# Revit family: MD2-OCRX2X2
name_source: partatom
category: Lighting Fixtures
units: mm (PartAtom-declared; Revit-internal decimal feet)

## family parameters
Always vertical = Yes
Cut with Voids When Loaded = No
Host = Ceiling
Light Source = Yes
OmniClass Number = 23.80.70.11.14.17
OmniClass Title = Direct/Indirect
Part Type = Normal
Room Calculation Point = No
Round Connector Dimension = Use Diameter
Shared = No

## types (12) — shared parameters
Assembly Code = D5020200
Color Filter = 16777215
Description = Patient Room Recessed Luminaire with Ambient and Examination Functions
Dimming Lamp Color Temperature Shift = <None>
Emit Shape Visible in Rendering = No
Emit from Rectangle Height = 0' - 1 15/32"
Emit from Rectangle Length = 1' - 11 11/16"
Emit from Rectangle Width = 1' - 11 3/4"
Housing Finish = Metal - Viscor - White
Lamp = LED
Length = 1' - 11 11/16"
Lens Depth = 0' - 1 15/32"
Lens Finish = Acrylic - Viscor - Opal White Square
Manufacturer = CERTOLUX by VISCOR
Model = MD2-OCRX
Tilt Angle = 90.00°
URL = https://www.viscor.com
Voltage = 120 V
Width = 1' - 11 3/4"

## per-type parameters (varying)
| type | Apparent Load | Lamp Wattage | Photometric Web File |
| MD2-OCRX 2X2-LED840K030L-840K040LUNV-C97(2) | 51 VA | 51 VA | MD2-OCRX 2X2-LED840K030L-840K040LUNV-C97(2).ies |
| MD2-OCRX 2X2-LED840K030L-840K050LUNV-C97(2) | 58 VA | 58 VA | MD2-OCRX 2X2-LED840K030L-840K050LUNV-C97(2).ies |
| MD2-OCRX 2X2-LED840K030L-840K060LUNV-C97(2) | 66 VA | 66 VA | MD2-OCRX 2X2-LED840K030L-840K060LUNV-C97(2).ies |
| MD2-OCRX 2X2-LED840K030L-840K075LUNV-C97(2) | 78 VA | 78 VA | MD2-OCRX 2X2-LED840K030L-840K075LUNV-C97(2).ies |
| MD2-OCRX 2X2-LED840K040L-840K040LUNV-C97(2) | 58 VA | 58 VA | MD2-OCRX 2X2-LED840K040L-840K040LUNV-C97(2).ies |
| MD2-OCRX 2X2-LED840K040L-840K050LUNV-C97(2) | 65 VA | 65 VA | MD2-OCRX 2X2-LED840K040L-840K050LUNV-C97(2).ies |
| MD2-OCRX 2X2-LED840K040L-840K060LUNV-C97(2) | 73 VA | 73 VA | MD2-OCRX 2X2-LED840K040L-840K060LUNV-C97(2).ies |
| MD2-OCRX 2X2-LED840K040L-840K075LUNV-C97(2) | 85 VA | 85 VA | MD2-OCRX 2X2-LED840K040L-840K075LUNV-C97(2).ies |
| MD2-OCRX 2X2-LED840K050L-840K040LUNV-C97(2) | 66 VA | 66 VA | MD2-OCRX 2X2-LED840K050L-840K040LUNV-C97(2).ies |
| MD2-OCRX 2X2-LED840K050L-840K050LUNV-C97(2) | 73 VA | 73 VA | MD2-OCRX 2X2-LED840K050L-840K050LUNV-C97(2).ies |
| MD2-OCRX 2X2-LED840K050L-840K060LUNV-C97(2) | 81 VA | 81 VA | MD2-OCRX 2X2-LED840K050L-840K060LUNV-C97(2).ies |
| MD2-OCRX 2X2-LED840K050L-840K075LUNV-C97(2) | 93 VA | 93 VA | MD2-OCRX 2X2-LED840K050L-840K075LUNV-C97(2).ies |

## geometry (parser evidence)
native form markers: Sweep x2
no freeform markers — native parametric forms only
